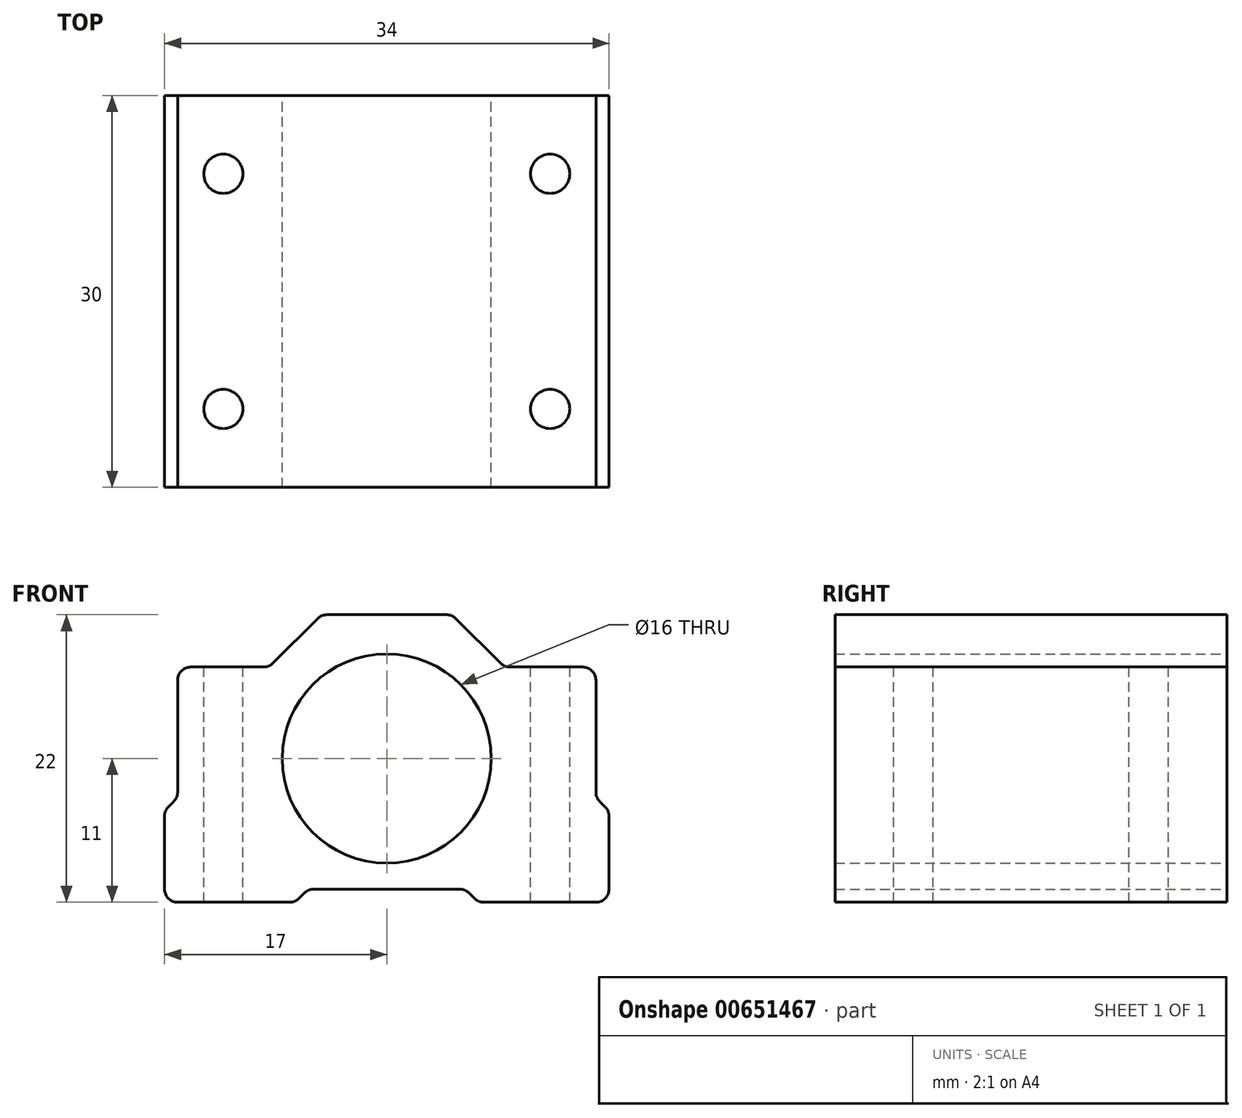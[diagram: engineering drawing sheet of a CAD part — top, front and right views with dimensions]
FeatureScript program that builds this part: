
annotation { "Feature Type Name" : "Feature", "Feature Type Description" : "" }
export const myFeature = defineFeature(function(context is Context, id is Id, definition is map)
    precondition{}
    {
        {
            var Q0;
            Q0=qCreatedBy(makeId("Front.planeOp"),FACE);
            var sketch = newSketch(context, id + "F0", { "sketchPlane" : qUnion([Q0])});
            skLineSegment(sketch, "E0.bottom", {"start": v(-16, -11) * mm, "end": v(-7.41, -11) * mm});
            skLineSegment(sketch, "E0.top", {"start": v(-4.59, 11) * mm, "end": v(4.59, 11) * mm});
            skLineSegment(sketch, "E0.left", {"start": v(-17, -10) * mm, "end": v(-17, -4.41) * mm});
            skLineSegment(sketch, "E0.right", {"start": v(17, -10) * mm, "end": v(17, -4.41) * mm});
            skCircle(sketch, "E1", {"center": v(0, 0) * mm, "radius": 8 * mm});
            skLineSegment(sketch, "E2", {"start": v(-5.59, -10) * mm, "end": v(5.59, -10) * mm});
            skLineSegment(sketch, "E3", {"start": v(-6.3, -10.3) * mm, "end": v(-6.7, -10.7) * mm});
            skLineSegment(sketch, "E4", {"start": v(6.3, -10.3) * mm, "end": v(6.7, -10.7) * mm});
            skLineSegment(sketch, "E5.trimOffspring", {"start": v(7.41, -11) * mm, "end": v(16, -11) * mm});
            skLineSegment(sketch, "E6", {"start": v(-5.3, 10.7) * mm, "end": v(-8.7, 7.3) * mm});
            skLineSegment(sketch, "E7", {"start": v(-9.41, 7) * mm, "end": v(-15, 7) * mm});
            skLineSegment(sketch, "E8", {"start": v(5.3, 10.7) * mm, "end": v(8.7, 7.3) * mm});
            skLineSegment(sketch, "E9", {"start": v(9.41, 7) * mm, "end": v(15, 7) * mm});
            skLineSegment(sketch, "E10", {"start": v(16, 6) * mm, "end": v(16, -2.59) * mm});
            skLineSegment(sketch, "E11", {"start": v(16.3, -3.3) * mm, "end": v(16.7, -3.7) * mm});
            skLineSegment(sketch, "E12", {"start": v(-16, 6) * mm, "end": v(-16, -2.59) * mm});
            skLineSegment(sketch, "E13", {"start": v(-16.3, -3.3) * mm, "end": v(-16.7, -3.7) * mm});
            skPoint(sketch, "E14.orphan", {"position": v(-17, 11) * mm});
            skPoint(sketch, "E15.orphan", {"position": v(-17, 7) * mm});
            skPoint(sketch, "E16.orphan", {"position": v(17, 7) * mm});
            skPoint(sketch, "E17.visualSharp", {"position": v(-16, 7) * mm});
            skArc(sketch, "E17.filletArc", {"start": v(-15, 7) * mm, "mid": v(-15.7, 6.7) * mm, "end": v(-16, 6) * mm});
            skPoint(sketch, "E18.visualSharp", {"position": v(-9, 7) * mm});
            skArc(sketch, "E18.filletArc", {"start": v(-9.41, 7) * mm, "mid": v(-9.03, 7.08) * mm, "end": v(-8.7, 7.3) * mm});
            skPoint(sketch, "E19.visualSharp", {"position": v(-5, 11) * mm});
            skArc(sketch, "E19.filletArc", {"start": v(-4.59, 11) * mm, "mid": v(-4.97, 10.92) * mm, "end": v(-5.3, 10.7) * mm});
            skPoint(sketch, "E20.visualSharp", {"position": v(5, 11) * mm});
            skArc(sketch, "E20.filletArc", {"start": v(5.3, 10.7) * mm, "mid": v(4.97, 10.92) * mm, "end": v(4.59, 11) * mm});
            skPoint(sketch, "E21.visualSharp", {"position": v(9, 7) * mm});
            skArc(sketch, "E21.filletArc", {"start": v(8.7, 7.3) * mm, "mid": v(9.03, 7.08) * mm, "end": v(9.41, 7) * mm});
            skPoint(sketch, "E22.visualSharp", {"position": v(16, 7) * mm});
            skArc(sketch, "E22.filletArc", {"start": v(16, 6) * mm, "mid": v(15.7, 6.7) * mm, "end": v(15, 7) * mm});
            skPoint(sketch, "E23.visualSharp", {"position": v(16, -3) * mm});
            skArc(sketch, "E23.filletArc", {"start": v(16, -2.59) * mm, "mid": v(16.08, -2.97) * mm, "end": v(16.3, -3.3) * mm});
            skPoint(sketch, "E24.visualSharp", {"position": v(17, -4) * mm});
            skArc(sketch, "E24.filletArc", {"start": v(17, -4.41) * mm, "mid": v(16.92, -4.03) * mm, "end": v(16.7, -3.7) * mm});
            skPoint(sketch, "E25.visualSharp", {"position": v(17, -11) * mm});
            skArc(sketch, "E25.filletArc", {"start": v(16, -11) * mm, "mid": v(16.7, -10.7) * mm, "end": v(17, -10) * mm});
            skPoint(sketch, "E26.visualSharp", {"position": v(7, -11) * mm});
            skArc(sketch, "E26.filletArc", {"start": v(6.7, -10.7) * mm, "mid": v(7.03, -10.92) * mm, "end": v(7.41, -11) * mm});
            skPoint(sketch, "E27.visualSharp", {"position": v(6, -10) * mm});
            skArc(sketch, "E27.filletArc", {"start": v(6.3, -10.3) * mm, "mid": v(5.97, -10.08) * mm, "end": v(5.59, -10) * mm});
            skPoint(sketch, "E28.visualSharp", {"position": v(-6, -10) * mm});
            skArc(sketch, "E28.filletArc", {"start": v(-5.59, -10) * mm, "mid": v(-5.97, -10.08) * mm, "end": v(-6.3, -10.3) * mm});
            skPoint(sketch, "E29.visualSharp", {"position": v(-7, -11) * mm});
            skArc(sketch, "E29.filletArc", {"start": v(-7.41, -11) * mm, "mid": v(-7.03, -10.92) * mm, "end": v(-6.7, -10.7) * mm});
            skPoint(sketch, "E30.visualSharp", {"position": v(-17, -11) * mm});
            skArc(sketch, "E30.filletArc", {"start": v(-17, -10) * mm, "mid": v(-16.7, -10.7) * mm, "end": v(-16, -11) * mm});
            skPoint(sketch, "E31.visualSharp", {"position": v(-17, -4) * mm});
            skArc(sketch, "E31.filletArc", {"start": v(-16.7, -3.7) * mm, "mid": v(-16.92, -4.03) * mm, "end": v(-17, -4.41) * mm});
            skPoint(sketch, "E32.visualSharp", {"position": v(-16, -3) * mm});
            skArc(sketch, "E32.filletArc", {"start": v(-16.3, -3.3) * mm, "mid": v(-16.08, -2.97) * mm, "end": v(-16, -2.59) * mm});
            skSolve(sketch);
        }
        {
            var Q0;
            Q0=makeQuery(id+"F0.imprint","IMPRINT",FACE,{"disambiguationData":[TD([[makeQuery(id+"F0.imprint","IMPRINT",EDGE,{"derivedFrom":sQuery(id+"F0.wireOp",EDGE,"E0.bottom")}),1.0]])]});
            extrude(context, id + "F1", {"entities" : qUnion([Q0]), "depth" : 30 * mm, "offsetDistance" : 25 * mm});
        }
        {
            var Q0;
            Q0=makeQuery(id+"F1.opExtrude","SWEPT_FACE",FACE,{"disambiguationData":[OSD([sQuery(id+"F0.wireOp",EDGE,"E9")])]});
            var sketch = newSketch(context, id + "F2", { "sketchPlane" : qUnion([Q0])});
            skCircle(sketch, "E33", {"center": v(-12.5, -6) * mm, "radius": 1.5 * mm});
            skCircle(sketch, "E34", {"center": v(-12.5, -24) * mm, "radius": 1.5 * mm});
            skCircle(sketch, "E35", {"center": v(12.5, -6) * mm, "radius": 1.5 * mm});
            skCircle(sketch, "E36", {"center": v(12.5, -24) * mm, "radius": 1.5 * mm});
            skSolve(sketch);
        }
        {
            var Q0;
            Q0 = qSketchRegion(id + "F2", true);
            extrude(context, id + "F3", {"entities" : qUnion([Q0]), "operationType" : NewBodyOperationType.REMOVE, "endBound" : BoundingType.THROUGH_ALL, "oppositeDirection" : true, "depth" : 25 * mm, "offsetDistance" : 25 * mm});
        }
    });
